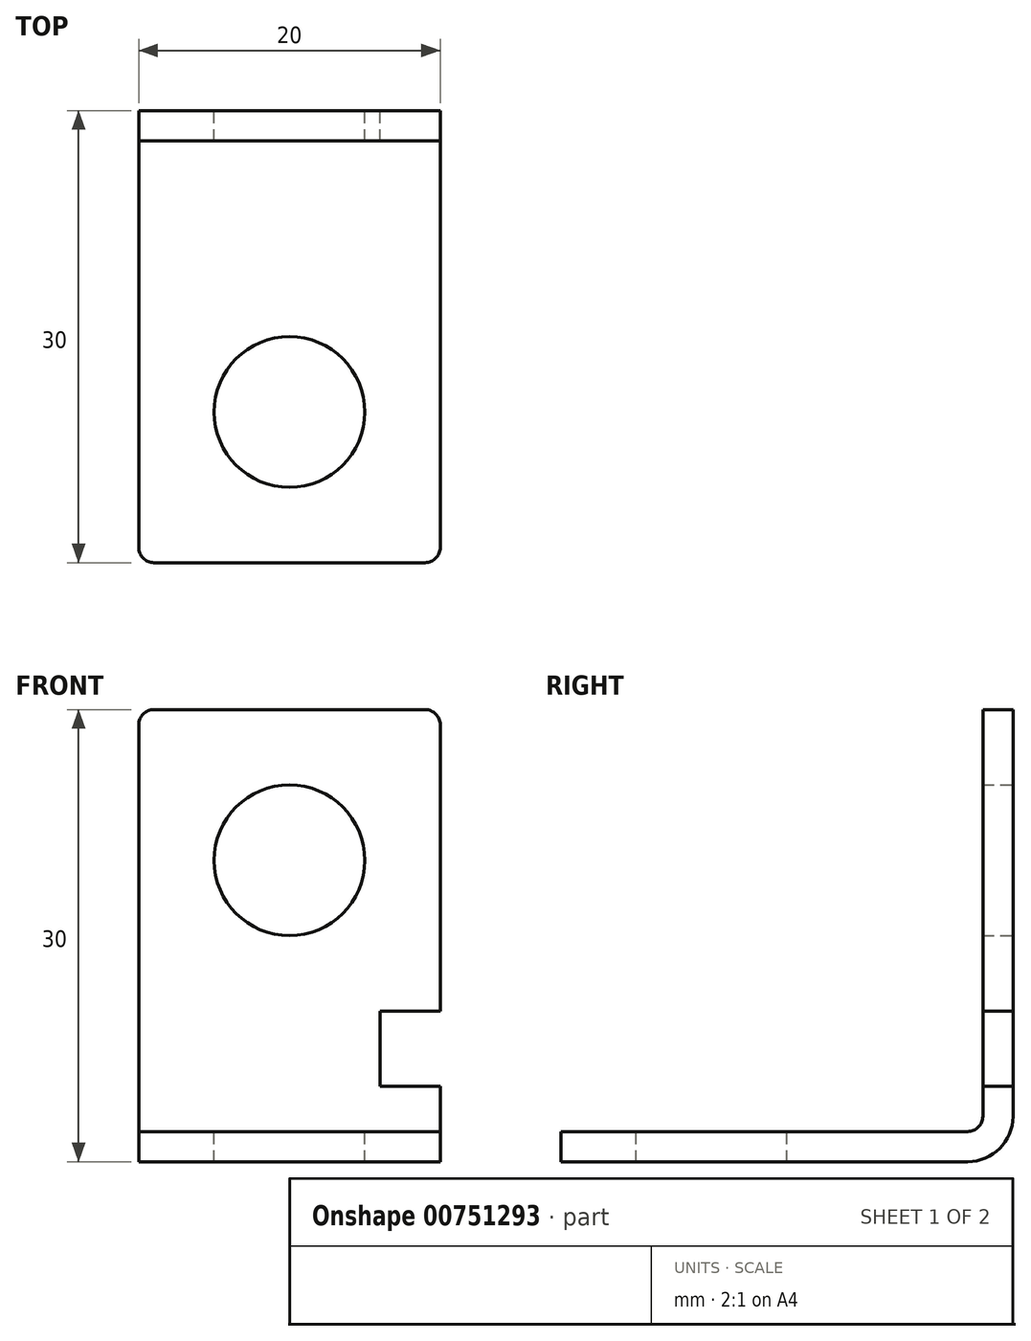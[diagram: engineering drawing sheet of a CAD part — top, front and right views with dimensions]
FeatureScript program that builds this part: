
annotation { "Feature Type Name" : "Feature", "Feature Type Description" : "" }
export const myFeature = defineFeature(function(context is Context, id is Id, definition is map)
    precondition{}
    {
        {
            var Q0;
            Q0=qCreatedBy(makeId("Front.planeOp"),FACE);
            var sketch = newSketch(context, id + "F0", { "sketchPlane" : qUnion([Q0])});
            skLineSegment(sketch, "E0", {"start": v(0, 0) * mm, "end": v(0, 30) * mm});
            skLineSegment(sketch, "E1", {"start": v(0, 30) * mm, "end": v(20, 30) * mm});
            skLineSegment(sketch, "E2", {"start": v(20, 30) * mm, "end": v(20, 0) * mm});
            skLineSegment(sketch, "E3", {"start": v(20, 0) * mm, "end": v(0, 0) * mm});
            skCircle(sketch, "E4", {"center": v(10, 20) * mm, "radius": 5 * mm});
            skPoint(sketch, "E4.centerSnap0", {"position": v(10, 30) * mm});
            skLineSegment(sketch, "E5", {"start": v(20, 10) * mm, "end": v(16, 10) * mm});
            skLineSegment(sketch, "E6", {"start": v(16, 10) * mm, "end": v(16, 5) * mm});
            skLineSegment(sketch, "E7", {"start": v(16, 5) * mm, "end": v(20, 5) * mm});
            skLineSegment(sketch, "E8", {"start": v(20, 5) * mm, "end": v(20, 10) * mm});
            skSolve(sketch);
        }
        {
            var Q0;
            Q0=makeQuery(id+"F0.imprint","IMPRINT",FACE,{"disambiguationData":[TD([[makeQuery(id+"F0.imprint","IMPRINT",EDGE,{"derivedFrom":sQuery(id+"F0.wireOp",EDGE,"E0")}),-1.0]])]});
            extrude(context, id + "F1", {"entities" : qUnion([Q0]), "depth" : 30 * mm, "offsetDistance" : 25 * mm});
        }
        {
            var Q0;
            Q0=makeQuery(id+"F1.opExtrude","SWEPT_FACE",FACE,{"disambiguationData":[OSD([sQuery(id+"F0.wireOp",EDGE,"E1")])]});
            var sketch = newSketch(context, id + "F2", { "sketchPlane" : qUnion([Q0])});
            skLineSegment(sketch, "E9", {"start": v(0, -2) * mm, "end": v(20, -2) * mm});
            skLineSegment(sketch, "E10", {"start": v(20, -2) * mm, "end": v(20, -30) * mm});
            skLineSegment(sketch, "E11", {"start": v(20, -30) * mm, "end": v(0, -30) * mm});
            skLineSegment(sketch, "E12", {"start": v(0, -30) * mm, "end": v(0, -2) * mm});
            skCircle(sketch, "E13", {"center": v(10, -20) * mm, "radius": 5 * mm});
            skPoint(sketch, "E13.centerSnap0", {"position": v(10, -30) * mm});
            skSolve(sketch);
        }
        {
            var Q0;
            Q0=makeQuery(id+"F2.imprint","IMPRINT",FACE,{"disambiguationData":[TD([[makeQuery(id+"F2.imprint","IMPRINT",EDGE,{"derivedFrom":sQuery(id+"F2.wireOp",EDGE,"E9")}),-1.0]])]});
            var Q1;
            Q1=makeQuery(id+"F2.imprint","IMPRINT",FACE,{"disambiguationData":[TD([[makeQuery(id+"F2.imprint","IMPRINT",EDGE,{"derivedFrom":sQuery(id+"F2.wireOp",EDGE,"E13")}),1.0]])]});
            extrude(context, id + "F3", {"entities" : qUnion([Q0, Q1]), "operationType" : NewBodyOperationType.REMOVE, "oppositeDirection" : true, "depth" : 28 * mm, "offsetDistance" : 25 * mm});
        }
        {
            var Q0;
            Q0=makeQuery(id+"F2.imprint","IMPRINT",FACE,{"disambiguationData":[TD([[makeQuery(id+"F2.imprint","IMPRINT",EDGE,{"derivedFrom":sQuery(id+"F2.wireOp",EDGE,"E13")}),1.0]])]});
            extrude(context, id + "F4", {"entities" : qUnion([Q0]), "operationType" : NewBodyOperationType.REMOVE, "oppositeDirection" : true, "depth" : 56 * mm, "offsetDistance" : 25 * mm});
        }
        {
            var Q0;
            {var subQ0=sQuery(id+"F0.wireOp",EDGE,"E2");Q0=makeQuery(id+"F1.opExtrude","CAP_EDGE",EDGE,{"disambiguationData":[OSD([subQ0]),TDD([makeQuery(id+"F0.imprint","IMPRINT",EDGE,{"disambiguationData":[TD([[makeQuery(id+"F0.imprint","INTERSECT",VERTEX,{"derivedFrom":[subQ0,sQuery(id+"F0.wireOp",EDGE,"E3")]}),1.0]])],"derivedFrom":subQ0})])],"isStart":false});}
            var Q1;
            Q1=makeQuery(id+"F1.opExtrude","CAP_EDGE",EDGE,{"disambiguationData":[OSD([sQuery(id+"F0.wireOp",EDGE,"E0")])],"isStart":false});
            var Q2;
            Q2=makeQuery(id+"F1.opExtrude","SWEPT_EDGE",EDGE,{"disambiguationData":[OSD([sQuery(id+"F0.wireOp",EDGE,"E1"),sQuery(id+"F0.wireOp",EDGE,"E2")])]});
            var Q3;
            Q3=makeQuery(id+"F1.opExtrude","SWEPT_EDGE",EDGE,{"disambiguationData":[OSD([sQuery(id+"F0.wireOp",EDGE,"E0"),sQuery(id+"F0.wireOp",EDGE,"E1")])]});
            fillet(context, id + "F5", {"entities" : qUnion([Q0, Q1, Q2, Q3]), "radius" : 1 * mm, "tangentPropagation" : true, "allowEdgeOverflow" : false});
        }
        {
            var Q0;
            Q0=makeQuery(id+"F1.opExtrude","CAP_EDGE",EDGE,{"disambiguationData":[OSD([sQuery(id+"F0.wireOp",EDGE,"E3")])],"isStart":true});
            fillet(context, id + "F6", {"entities" : qUnion([Q0]), "radius" : 3 * mm, "tangentPropagation" : true, "allowEdgeOverflow" : false});
        }
        {
            var Q0;
            Q0=makeQuery(id+"F3.boolean.opBoolean","COPY",EDGE,{"derivedFrom":makeQuery(id+"F3.opExtrude","CAP_EDGE",EDGE,{"disambiguationData":[OSD([sQuery(id+"F2.wireOp",EDGE,"E9")])],"isStart":false})});
            fillet(context, id + "F7", {"entities" : qUnion([Q0]), "radius" : 1 * mm, "tangentPropagation" : true, "allowEdgeOverflow" : false});
        }
    });
